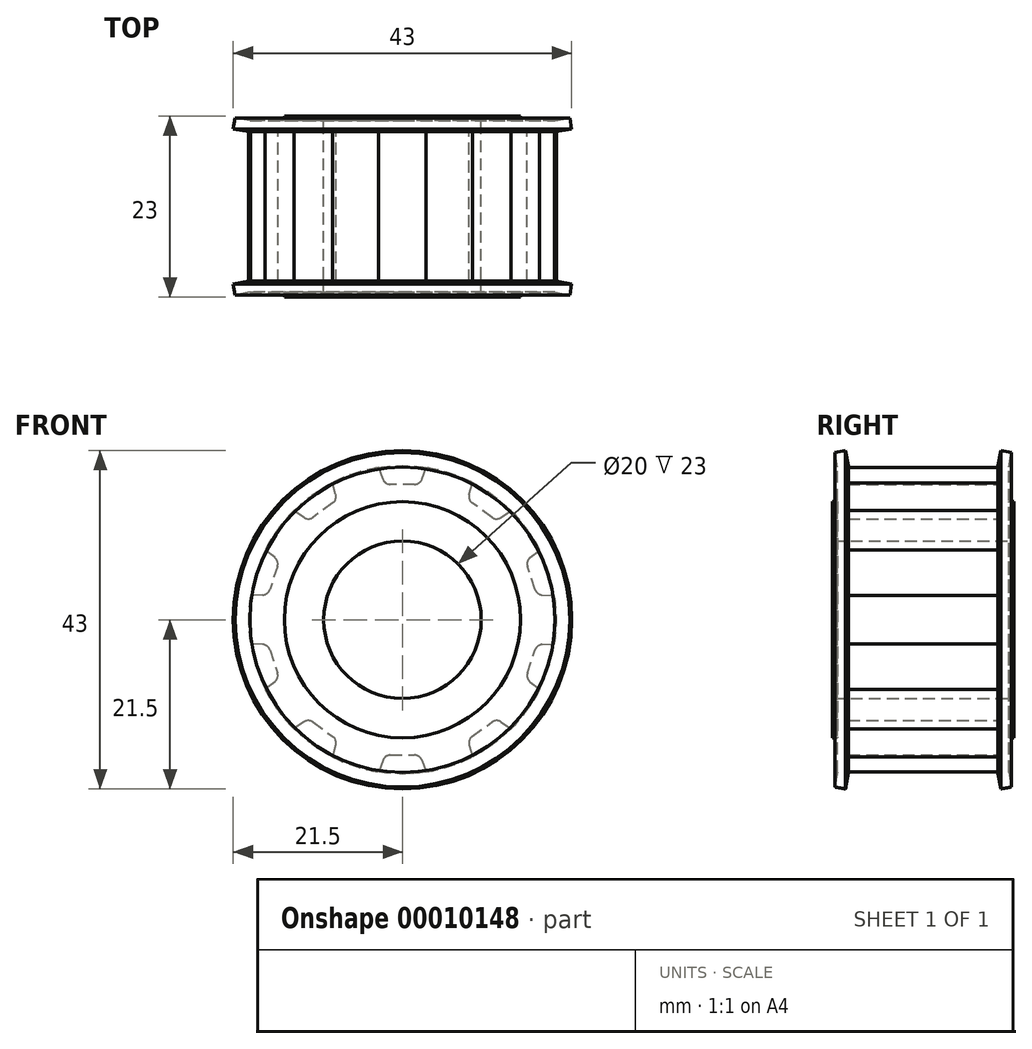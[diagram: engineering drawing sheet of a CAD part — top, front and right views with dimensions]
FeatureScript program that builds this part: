
annotation { "Feature Type Name" : "Feature", "Feature Type Description" : "" }
export const myFeature = defineFeature(function(context is Context, id is Id, definition is map)
    precondition{}
    {
        {
            var Q0;
            Q0=qCreatedBy(makeId("Front.planeOp"),FACE);
            var sketch = newSketch(context, id + "F0", { "sketchPlane" : qUnion([Q0])});
            skCircle(sketch, "E0", {"center": v(0, 0) * mm, "radius": 19.55 * mm, "construction": true});
            skCircle(sketch, "E1", {"center": v(0, 0) * mm, "radius": 15 * mm, "construction": true});
            skCircle(sketch, "E2", {"center": v(0, 0) * mm, "radius": 10 * mm, "construction": true});
            skSolve(sketch);
        }
        {
            var Q0;
            Q0=qCreatedBy(makeId("Front.planeOp"),FACE);
            var sketch = newSketch(context, id + "F1", { "sketchPlane" : qUnion([Q0])});
            skLineSegment(sketch, "E3", {"start": v(1.55, 17.2) * mm, "end": v(-1.55, 17.2) * mm});
            skLineSegment(sketch, "E4", {"start": v(-2.49, 17.86) * mm, "end": v(-3.02, 19.32) * mm});
            skLineSegment(sketch, "E5", {"start": v(2.49, 17.86) * mm, "end": v(3.02, 19.32) * mm});
            skLineSegment(sketch, "E6", {"start": v(0, 0) * mm, "end": v(0, 25.93) * mm, "construction": true});
            skPoint(sketch, "E7.visualSharp", {"position": v(2.25, 17.2) * mm});
            skArc(sketch, "E7.filletArc", {"start": v(1.55, 17.2) * mm, "mid": v(2.12, 17.38) * mm, "end": v(2.49, 17.86) * mm});
            skPoint(sketch, "E8.visualSharp", {"position": v(-2.25, 17.2) * mm});
            skArc(sketch, "E8.filletArc", {"start": v(-2.49, 17.86) * mm, "mid": v(-2.12, 17.38) * mm, "end": v(-1.55, 17.2) * mm});
            skArc(sketch, "E9.0", {"start": v(8.9, 17.4) * mm, "mid": v(6.04, 18.6) * mm, "end": v(3.02, 19.32) * mm});
            skLineSegment(sketch, "E10.1.0", {"start": v(-8.48, 15.91) * mm, "end": v(-8.9, 17.4) * mm});
            skArc(sketch, "E10.1.1", {"start": v(-8.86, 14.83) * mm, "mid": v(-8.5, 15.3) * mm, "end": v(-8.48, 15.91) * mm});
            skLineSegment(sketch, "E10.1.2", {"start": v(-8.86, 14.83) * mm, "end": v(-11.36, 13) * mm});
            skArc(sketch, "E10.1.3", {"start": v(-12.51, 12.98) * mm, "mid": v(-11.93, 12.81) * mm, "end": v(-11.36, 13) * mm});
            skLineSegment(sketch, "E10.1.4", {"start": v(-12.51, 12.98) * mm, "end": v(-13.8, 13.85) * mm});
            skLineSegment(sketch, "E10.2.0", {"start": v(-16.21, 7.89) * mm, "end": v(-17.44, 8.84) * mm});
            skArc(sketch, "E10.2.1", {"start": v(-15.88, 6.79) * mm, "mid": v(-15.87, 7.4) * mm, "end": v(-16.21, 7.89) * mm});
            skLineSegment(sketch, "E10.2.2", {"start": v(-15.88, 6.79) * mm, "end": v(-16.84, 3.84) * mm});
            skArc(sketch, "E10.2.3", {"start": v(-17.75, 3.15) * mm, "mid": v(-17.19, 3.35) * mm, "end": v(-16.84, 3.84) * mm});
            skLineSegment(sketch, "E10.2.4", {"start": v(-17.75, 3.15) * mm, "end": v(-19.3, 3.1) * mm});
            skLineSegment(sketch, "E10.3.0", {"start": v(-17.75, -3.15) * mm, "end": v(-19.3, -3.1) * mm});
            skArc(sketch, "E10.3.1", {"start": v(-16.84, -3.84) * mm, "mid": v(-17.19, -3.35) * mm, "end": v(-17.75, -3.15) * mm});
            skLineSegment(sketch, "E10.3.2", {"start": v(-16.84, -3.84) * mm, "end": v(-15.88, -6.79) * mm});
            skArc(sketch, "E10.3.3", {"start": v(-16.21, -7.89) * mm, "mid": v(-15.87, -7.4) * mm, "end": v(-15.88, -6.79) * mm});
            skLineSegment(sketch, "E10.3.4", {"start": v(-16.21, -7.89) * mm, "end": v(-17.44, -8.84) * mm});
            skLineSegment(sketch, "E10.4.0", {"start": v(-12.51, -12.98) * mm, "end": v(-13.8, -13.85) * mm});
            skArc(sketch, "E10.4.1", {"start": v(-11.36, -13) * mm, "mid": v(-11.93, -12.81) * mm, "end": v(-12.51, -12.98) * mm});
            skLineSegment(sketch, "E10.4.2", {"start": v(-11.36, -13) * mm, "end": v(-8.86, -14.83) * mm});
            skArc(sketch, "E10.4.3", {"start": v(-8.48, -15.91) * mm, "mid": v(-8.5, -15.3) * mm, "end": v(-8.86, -14.83) * mm});
            skLineSegment(sketch, "E10.4.4", {"start": v(-8.48, -15.91) * mm, "end": v(-8.9, -17.4) * mm});
            skLineSegment(sketch, "E10.5.0", {"start": v(-2.49, -17.86) * mm, "end": v(-3.02, -19.32) * mm});
            skArc(sketch, "E10.5.1", {"start": v(-1.55, -17.2) * mm, "mid": v(-2.12, -17.38) * mm, "end": v(-2.49, -17.86) * mm});
            skLineSegment(sketch, "E10.5.2", {"start": v(-1.55, -17.2) * mm, "end": v(1.55, -17.2) * mm});
            skArc(sketch, "E10.5.3", {"start": v(2.49, -17.86) * mm, "mid": v(2.12, -17.38) * mm, "end": v(1.55, -17.2) * mm});
            skLineSegment(sketch, "E10.5.4", {"start": v(2.49, -17.86) * mm, "end": v(3.02, -19.32) * mm});
            skLineSegment(sketch, "E10.6.0", {"start": v(8.48, -15.91) * mm, "end": v(8.9, -17.4) * mm});
            skArc(sketch, "E10.6.1", {"start": v(8.86, -14.83) * mm, "mid": v(8.5, -15.3) * mm, "end": v(8.48, -15.91) * mm});
            skLineSegment(sketch, "E10.6.2", {"start": v(8.86, -14.83) * mm, "end": v(11.36, -13) * mm});
            skArc(sketch, "E10.6.3", {"start": v(12.51, -12.98) * mm, "mid": v(11.93, -12.81) * mm, "end": v(11.36, -13) * mm});
            skLineSegment(sketch, "E10.6.4", {"start": v(12.51, -12.98) * mm, "end": v(13.8, -13.85) * mm});
            skLineSegment(sketch, "E10.7.0", {"start": v(16.21, -7.89) * mm, "end": v(17.44, -8.84) * mm});
            skArc(sketch, "E10.7.1", {"start": v(15.88, -6.79) * mm, "mid": v(15.87, -7.4) * mm, "end": v(16.21, -7.89) * mm});
            skLineSegment(sketch, "E10.7.2", {"start": v(15.88, -6.79) * mm, "end": v(16.84, -3.84) * mm});
            skArc(sketch, "E10.7.3", {"start": v(17.75, -3.15) * mm, "mid": v(17.19, -3.35) * mm, "end": v(16.84, -3.84) * mm});
            skLineSegment(sketch, "E10.7.4", {"start": v(17.75, -3.15) * mm, "end": v(19.3, -3.1) * mm});
            skLineSegment(sketch, "E10.8.0", {"start": v(17.75, 3.15) * mm, "end": v(19.3, 3.1) * mm});
            skArc(sketch, "E10.8.1", {"start": v(16.84, 3.84) * mm, "mid": v(17.19, 3.35) * mm, "end": v(17.75, 3.15) * mm});
            skLineSegment(sketch, "E10.8.2", {"start": v(16.84, 3.84) * mm, "end": v(15.88, 6.79) * mm});
            skArc(sketch, "E10.8.3", {"start": v(16.21, 7.89) * mm, "mid": v(15.87, 7.4) * mm, "end": v(15.88, 6.79) * mm});
            skLineSegment(sketch, "E10.8.4", {"start": v(16.21, 7.89) * mm, "end": v(17.44, 8.84) * mm});
            skLineSegment(sketch, "E10.9.0", {"start": v(12.51, 12.98) * mm, "end": v(13.8, 13.85) * mm});
            skArc(sketch, "E10.9.1", {"start": v(11.36, 13) * mm, "mid": v(11.93, 12.81) * mm, "end": v(12.51, 12.98) * mm});
            skLineSegment(sketch, "E10.9.2", {"start": v(11.36, 13) * mm, "end": v(8.86, 14.83) * mm});
            skArc(sketch, "E10.9.3", {"start": v(8.48, 15.91) * mm, "mid": v(8.5, 15.3) * mm, "end": v(8.86, 14.83) * mm});
            skLineSegment(sketch, "E10.9.4", {"start": v(8.48, 15.91) * mm, "end": v(8.9, 17.4) * mm});
            skArc(sketch, "E11.trimOffspring", {"start": v(17.44, 8.84) * mm, "mid": v(15.82, 11.5) * mm, "end": v(13.8, 13.85) * mm});
            skArc(sketch, "E12.trimOffspring", {"start": v(19.3, -3.1) * mm, "mid": v(19.55, 0) * mm, "end": v(19.3, 3.1) * mm});
            skArc(sketch, "E13.trimOffspring", {"start": v(13.8, -13.85) * mm, "mid": v(15.82, -11.5) * mm, "end": v(17.44, -8.84) * mm});
            skArc(sketch, "E14.trimOffspring", {"start": v(3.02, -19.32) * mm, "mid": v(6.04, -18.6) * mm, "end": v(8.9, -17.4) * mm});
            skArc(sketch, "E15.trimOffspring", {"start": v(-8.9, -17.4) * mm, "mid": v(-6.04, -18.6) * mm, "end": v(-3.02, -19.32) * mm});
            skArc(sketch, "E16.trimOffspring", {"start": v(-17.44, -8.84) * mm, "mid": v(-15.82, -11.5) * mm, "end": v(-13.8, -13.85) * mm});
            skArc(sketch, "E17.trimOffspring", {"start": v(-19.3, 3.1) * mm, "mid": v(-19.55, 0) * mm, "end": v(-19.3, -3.1) * mm});
            skArc(sketch, "E18.trimOffspring", {"start": v(-13.8, 13.85) * mm, "mid": v(-15.82, 11.5) * mm, "end": v(-17.44, 8.84) * mm});
            skArc(sketch, "E19.trimOffspring", {"start": v(-3.02, 19.32) * mm, "mid": v(-6.04, 18.6) * mm, "end": v(-8.9, 17.4) * mm});
            skSolve(sketch);
        }
        {
            var Q0;
            Q0 = qSketchRegion(id + "F1", true);
            extrude(context, id + "F2", {"entities" : qUnion([Q0]), "endBound" : BoundingType.SYMMETRIC, "depth" : 19 * mm});
        }
        {
            var Q0;
            Q0=makeQuery(id+"F2.opExtrude","CAP_FACE",FACE,{"disambiguationData":[OSD([sQuery(id+"F1.wireOp",EDGE,"E3"),sQuery(id+"F1.wireOp",EDGE,"E4"),sQuery(id+"F1.wireOp",EDGE,"E5"),sQuery(id+"F1.wireOp",EDGE,"E7.filletArc"),sQuery(id+"F1.wireOp",EDGE,"E8.filletArc"),sQuery(id+"F1.wireOp",EDGE,"E9.0"),sQuery(id+"F1.wireOp",EDGE,"E10.1.0"),sQuery(id+"F1.wireOp",EDGE,"E10.1.1"),sQuery(id+"F1.wireOp",EDGE,"E10.1.2"),sQuery(id+"F1.wireOp",EDGE,"E10.1.3"),sQuery(id+"F1.wireOp",EDGE,"E10.1.4"),sQuery(id+"F1.wireOp",EDGE,"E10.2.0"),sQuery(id+"F1.wireOp",EDGE,"E10.2.1"),sQuery(id+"F1.wireOp",EDGE,"E10.2.2"),sQuery(id+"F1.wireOp",EDGE,"E10.2.3"),sQuery(id+"F1.wireOp",EDGE,"E10.2.4"),sQuery(id+"F1.wireOp",EDGE,"E10.3.0"),sQuery(id+"F1.wireOp",EDGE,"E10.3.1"),sQuery(id+"F1.wireOp",EDGE,"E10.3.2"),sQuery(id+"F1.wireOp",EDGE,"E10.3.3"),sQuery(id+"F1.wireOp",EDGE,"E10.3.4"),sQuery(id+"F1.wireOp",EDGE,"E10.4.0"),sQuery(id+"F1.wireOp",EDGE,"E10.4.1"),sQuery(id+"F1.wireOp",EDGE,"E10.4.2"),sQuery(id+"F1.wireOp",EDGE,"E10.4.3"),sQuery(id+"F1.wireOp",EDGE,"E10.4.4"),sQuery(id+"F1.wireOp",EDGE,"E10.5.0"),sQuery(id+"F1.wireOp",EDGE,"E10.5.1"),sQuery(id+"F1.wireOp",EDGE,"E10.5.2"),sQuery(id+"F1.wireOp",EDGE,"E10.5.3"),sQuery(id+"F1.wireOp",EDGE,"E10.5.4"),sQuery(id+"F1.wireOp",EDGE,"E10.6.0"),sQuery(id+"F1.wireOp",EDGE,"E10.6.1"),sQuery(id+"F1.wireOp",EDGE,"E10.6.2"),sQuery(id+"F1.wireOp",EDGE,"E10.6.3"),sQuery(id+"F1.wireOp",EDGE,"E10.6.4"),sQuery(id+"F1.wireOp",EDGE,"E10.7.0"),sQuery(id+"F1.wireOp",EDGE,"E10.7.1"),sQuery(id+"F1.wireOp",EDGE,"E10.7.2"),sQuery(id+"F1.wireOp",EDGE,"E10.7.3"),sQuery(id+"F1.wireOp",EDGE,"E10.7.4"),sQuery(id+"F1.wireOp",EDGE,"E10.8.0"),sQuery(id+"F1.wireOp",EDGE,"E10.8.1"),sQuery(id+"F1.wireOp",EDGE,"E10.8.2"),sQuery(id+"F1.wireOp",EDGE,"E10.8.3"),sQuery(id+"F1.wireOp",EDGE,"E10.8.4"),sQuery(id+"F1.wireOp",EDGE,"E10.9.0"),sQuery(id+"F1.wireOp",EDGE,"E10.9.1"),sQuery(id+"F1.wireOp",EDGE,"E10.9.2"),sQuery(id+"F1.wireOp",EDGE,"E10.9.3"),sQuery(id+"F1.wireOp",EDGE,"E10.9.4"),sQuery(id+"F1.wireOp",EDGE,"E11.trimOffspring"),sQuery(id+"F1.wireOp",EDGE,"E12.trimOffspring"),sQuery(id+"F1.wireOp",EDGE,"E13.trimOffspring"),sQuery(id+"F1.wireOp",EDGE,"E14.trimOffspring"),sQuery(id+"F1.wireOp",EDGE,"E15.trimOffspring"),sQuery(id+"F1.wireOp",EDGE,"E16.trimOffspring"),sQuery(id+"F1.wireOp",EDGE,"E17.trimOffspring"),sQuery(id+"F1.wireOp",EDGE,"E18.trimOffspring"),sQuery(id+"F1.wireOp",EDGE,"E19.trimOffspring")])],"isStart":false});
            var sketch = newSketch(context, id + "F3", { "sketchPlane" : qUnion([Q0])});
            skCircle(sketch, "E20.0", {"center": v(0, 0) * mm, "radius": 15 * mm});
            skSolve(sketch);
        }
        {
            var Q0;
            Q0 = qSketchRegion(id + "F3", true);
            extrude(context, id + "F4", {"entities" : qUnion([Q0]), "operationType" : NewBodyOperationType.ADD, "depth" : 2 * mm});
        }
        {
            var Q0;
            Q0=makeQuery(id+"F2.opExtrude","CAP_FACE",FACE,{"disambiguationData":[OSD([sQuery(id+"F1.wireOp",EDGE,"E3"),sQuery(id+"F1.wireOp",EDGE,"E4"),sQuery(id+"F1.wireOp",EDGE,"E5"),sQuery(id+"F1.wireOp",EDGE,"E7.filletArc"),sQuery(id+"F1.wireOp",EDGE,"E8.filletArc"),sQuery(id+"F1.wireOp",EDGE,"E9.0"),sQuery(id+"F1.wireOp",EDGE,"E10.1.0"),sQuery(id+"F1.wireOp",EDGE,"E10.1.1"),sQuery(id+"F1.wireOp",EDGE,"E10.1.2"),sQuery(id+"F1.wireOp",EDGE,"E10.1.3"),sQuery(id+"F1.wireOp",EDGE,"E10.1.4"),sQuery(id+"F1.wireOp",EDGE,"E10.2.0"),sQuery(id+"F1.wireOp",EDGE,"E10.2.1"),sQuery(id+"F1.wireOp",EDGE,"E10.2.2"),sQuery(id+"F1.wireOp",EDGE,"E10.2.3"),sQuery(id+"F1.wireOp",EDGE,"E10.2.4"),sQuery(id+"F1.wireOp",EDGE,"E10.3.0"),sQuery(id+"F1.wireOp",EDGE,"E10.3.1"),sQuery(id+"F1.wireOp",EDGE,"E10.3.2"),sQuery(id+"F1.wireOp",EDGE,"E10.3.3"),sQuery(id+"F1.wireOp",EDGE,"E10.3.4"),sQuery(id+"F1.wireOp",EDGE,"E10.4.0"),sQuery(id+"F1.wireOp",EDGE,"E10.4.1"),sQuery(id+"F1.wireOp",EDGE,"E10.4.2"),sQuery(id+"F1.wireOp",EDGE,"E10.4.3"),sQuery(id+"F1.wireOp",EDGE,"E10.4.4"),sQuery(id+"F1.wireOp",EDGE,"E10.5.0"),sQuery(id+"F1.wireOp",EDGE,"E10.5.1"),sQuery(id+"F1.wireOp",EDGE,"E10.5.2"),sQuery(id+"F1.wireOp",EDGE,"E10.5.3"),sQuery(id+"F1.wireOp",EDGE,"E10.5.4"),sQuery(id+"F1.wireOp",EDGE,"E10.6.0"),sQuery(id+"F1.wireOp",EDGE,"E10.6.1"),sQuery(id+"F1.wireOp",EDGE,"E10.6.2"),sQuery(id+"F1.wireOp",EDGE,"E10.6.3"),sQuery(id+"F1.wireOp",EDGE,"E10.6.4"),sQuery(id+"F1.wireOp",EDGE,"E10.7.0"),sQuery(id+"F1.wireOp",EDGE,"E10.7.1"),sQuery(id+"F1.wireOp",EDGE,"E10.7.2"),sQuery(id+"F1.wireOp",EDGE,"E10.7.3"),sQuery(id+"F1.wireOp",EDGE,"E10.7.4"),sQuery(id+"F1.wireOp",EDGE,"E10.8.0"),sQuery(id+"F1.wireOp",EDGE,"E10.8.1"),sQuery(id+"F1.wireOp",EDGE,"E10.8.2"),sQuery(id+"F1.wireOp",EDGE,"E10.8.3"),sQuery(id+"F1.wireOp",EDGE,"E10.8.4"),sQuery(id+"F1.wireOp",EDGE,"E10.9.0"),sQuery(id+"F1.wireOp",EDGE,"E10.9.1"),sQuery(id+"F1.wireOp",EDGE,"E10.9.2"),sQuery(id+"F1.wireOp",EDGE,"E10.9.3"),sQuery(id+"F1.wireOp",EDGE,"E10.9.4"),sQuery(id+"F1.wireOp",EDGE,"E11.trimOffspring"),sQuery(id+"F1.wireOp",EDGE,"E12.trimOffspring"),sQuery(id+"F1.wireOp",EDGE,"E13.trimOffspring"),sQuery(id+"F1.wireOp",EDGE,"E14.trimOffspring"),sQuery(id+"F1.wireOp",EDGE,"E15.trimOffspring"),sQuery(id+"F1.wireOp",EDGE,"E16.trimOffspring"),sQuery(id+"F1.wireOp",EDGE,"E17.trimOffspring"),sQuery(id+"F1.wireOp",EDGE,"E18.trimOffspring"),sQuery(id+"F1.wireOp",EDGE,"E19.trimOffspring")])],"isStart":true});
            var sketch = newSketch(context, id + "F5", { "sketchPlane" : qUnion([Q0])});
            skCircle(sketch, "E21.0", {"center": v(0, 0) * mm, "radius": 15 * mm});
            skSolve(sketch);
        }
        {
            var Q0;
            Q0 = qSketchRegion(id + "F5", true);
            extrude(context, id + "F6", {"entities" : qUnion([Q0]), "operationType" : NewBodyOperationType.ADD, "depth" : 2 * mm});
        }
        {
            var Q0;
            Q0=makeQuery(id+"F6.opExtrude","CAP_FACE",FACE,{"disambiguationData":[OSD([sQuery(id+"F5.wireOp",EDGE,"E21.0")])],"isStart":false});
            var sketch = newSketch(context, id + "F7", { "sketchPlane" : qUnion([Q0])});
            skCircle(sketch, "E22.0", {"center": v(0, 0) * mm, "radius": 10 * mm});
            skSolve(sketch);
        }
        {
            var Q0;
            Q0 = qSketchRegion(id + "F7", true);
            extrude(context, id + "F8", {"entities" : qUnion([Q0]), "operationType" : NewBodyOperationType.REMOVE, "oppositeDirection" : true, "depth" : 25 * mm});
        }
        {
            var Q0;
            Q0=qCreatedBy(makeId("Right.planeOp"),FACE);
            var sketch = newSketch(context, id + "F9", { "sketchPlane" : qUnion([Q0])});
            skLineSegment(sketch, "E23", {"start": v(-10.9, -15) * mm, "end": v(-9.5, -15) * mm});
            skLineSegment(sketch, "E24", {"start": v(-9.5, -15) * mm, "end": v(-9.5, -19.5) * mm});
            skLineSegment(sketch, "E25", {"start": v(-9.5, -19.5) * mm, "end": v(-9.85, -21.5) * mm});
            skLineSegment(sketch, "E26", {"start": v(-9.85, -21.5) * mm, "end": v(-11.23, -21.26) * mm});
            skLineSegment(sketch, "E27", {"start": v(-11.23, -21.26) * mm, "end": v(-10.9, -19.38) * mm});
            skLineSegment(sketch, "E28", {"start": v(-10.9, -19.38) * mm, "end": v(-10.9, -15) * mm});
            skLineSegment(sketch, "E29.0.MirrorCS", {"start": v(10.9, -19.38) * mm, "end": v(10.9, -15) * mm});
            skLineSegment(sketch, "E30.0.MirrorCS", {"start": v(10.9, -15) * mm, "end": v(9.5, -15) * mm});
            skLineSegment(sketch, "E31.0.MirrorCS", {"start": v(9.5, -15) * mm, "end": v(9.5, -19.5) * mm});
            skLineSegment(sketch, "E32.0.MirrorCS", {"start": v(9.5, -19.5) * mm, "end": v(9.85, -21.5) * mm});
            skLineSegment(sketch, "E33.0.MirrorCS", {"start": v(11.23, -21.26) * mm, "end": v(10.9, -19.38) * mm});
            skLineSegment(sketch, "E34.0.MirrorCS", {"start": v(9.85, -21.5) * mm, "end": v(11.23, -21.26) * mm});
            skLineSegment(sketch, "E35", {"start": v(0, 0) * mm, "end": v(18.13, 0) * mm, "construction": true});
            skSolve(sketch);
        }
        {
            var Q0;
            Q0 = qSketchRegion(id + "F9", true);
            var Q1;
            Q1=sQuery(id+"F9.wireOp",EDGE,"E35");
            revolve(context, id + "F10", {"operationType" : NewBodyOperationType.ADD, "entities" : qUnion([Q0]), "axis" : qUnion([Q1]), "revolveType" : RevolveType.FULL});
        }
    });
